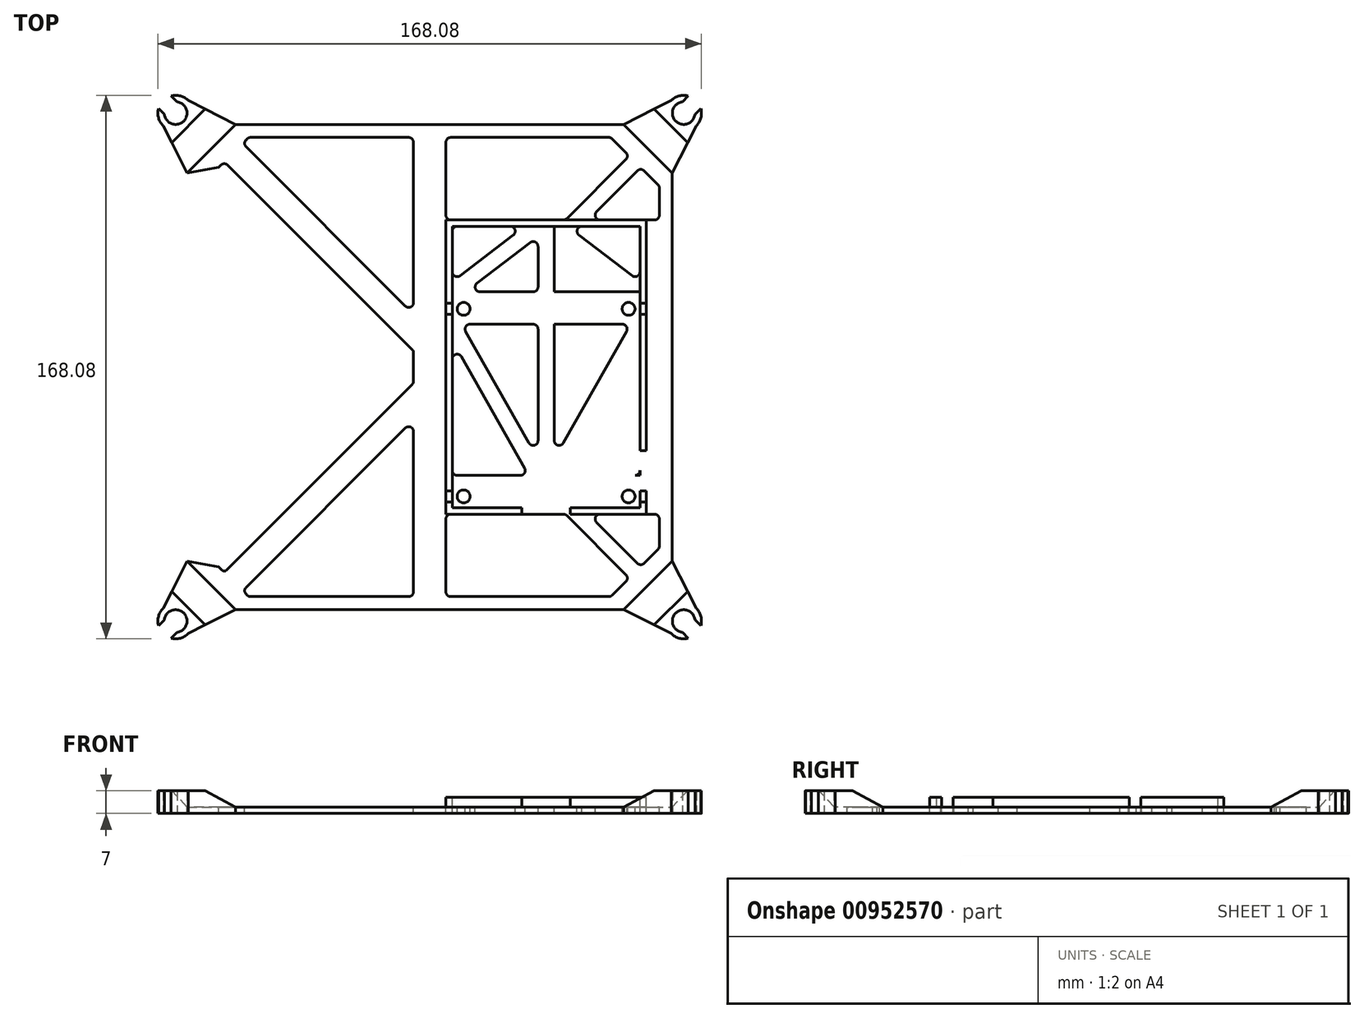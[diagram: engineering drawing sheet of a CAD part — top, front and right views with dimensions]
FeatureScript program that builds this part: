
annotation { "Feature Type Name" : "Feature", "Feature Type Description" : "" }
export const myFeature = defineFeature(function(context is Context, id is Id, definition is map)
    precondition{}
    {
        {
            var Q0;
            Q0=qCreatedBy(makeId("Top.planeOp"),FACE);
            var sketch = newSketch(context, id + "F0", { "sketchPlane" : qUnion([Q0])});
            skLineSegment(sketch, "E0.bottom", {"start": v(-75, 75) * mm, "end": v(75, 75) * mm});
            skLineSegment(sketch, "E0.top", {"start": v(-75, -75) * mm, "end": v(75, -75) * mm});
            skLineSegment(sketch, "E0.left", {"start": v(-75, 75) * mm, "end": v(-75, -75) * mm});
            skLineSegment(sketch, "E0.right", {"start": v(75, 75) * mm, "end": v(75, -75) * mm});
            skPoint(sketch, "E1", {"position": v(0, 75) * mm});
            skPoint(sketch, "E2", {"position": v(-75, 0) * mm});
            skSolve(sketch);
        }
        {
            var Q0;
            Q0=qSketchRegion(id+"F0",true);
            extrude(context, id + "F1", {"entities" : qUnion([Q0]), "depth" : 2 * mm, "offsetDistance" : 25 * mm});
        }
        {
            var Q0;
            Q0=makeQuery(id+"F1.opExtrude","CAP_FACE",FACE,{"disambiguationData":[OSD([sQuery(id+"F0.wireOp",EDGE,"E0.bottom"),sQuery(id+"F0.wireOp",EDGE,"E0.top"),sQuery(id+"F0.wireOp",EDGE,"E0.left"),sQuery(id+"F0.wireOp",EDGE,"E0.right")])],"isStart":false});
            var sketch = newSketch(context, id + "F2", { "sketchPlane" : qUnion([Q0])});
            skLineSegment(sketch, "E3.bottom", {"start": v(7, 43.5) * mm, "end": v(65, 43.5) * mm});
            skLineSegment(sketch, "E3.top", {"start": v(7, -43.5) * mm, "end": v(65, -43.5) * mm});
            skLineSegment(sketch, "E3.left", {"start": v(7, 43.5) * mm, "end": v(7, -43.5) * mm});
            skLineSegment(sketch, "E3.right", {"start": v(65, 43.5) * mm, "end": v(65, -43.5) * mm});
            skPoint(sketch, "E4", {"position": v(36, 43.5) * mm});
            skLineSegment(sketch, "E5.0", {"start": v(5, 45.5) * mm, "end": v(67, 45.5) * mm});
            skLineSegment(sketch, "E5.1", {"start": v(5, 45.5) * mm, "end": v(5, -45.5) * mm});
            skLineSegment(sketch, "E5.2", {"start": v(5, -45.5) * mm, "end": v(67, -45.5) * mm});
            skLineSegment(sketch, "E5.3", {"start": v(67, 45.5) * mm, "end": v(67, -45.5) * mm});
            skPoint(sketch, "E6", {"position": v(7, 0) * mm});
            skSolve(sketch);
        }
        {
            var Q0;
            Q0=qSketchRegion(id+"F2",true);
            extrude(context, id + "F3", {"entities" : qUnion([Q0]), "operationType" : NewBodyOperationType.ADD, "depth" : 3 * mm, "offsetDistance" : 25 * mm});
        }
        {
            var Q0;
            Q0=makeQuery(id+"F3.opExtrude","CAP_FACE",FACE,{"disambiguationData":[OSD([sQuery(id+"F2.wireOp",EDGE,"E3.bottom"),sQuery(id+"F2.wireOp",EDGE,"E3.top"),sQuery(id+"F2.wireOp",EDGE,"E3.left"),sQuery(id+"F2.wireOp",EDGE,"E3.right"),sQuery(id+"F2.wireOp",EDGE,"E5.0"),sQuery(id+"F2.wireOp",EDGE,"E5.1"),sQuery(id+"F2.wireOp",EDGE,"E5.2"),sQuery(id+"F2.wireOp",EDGE,"E5.3")])],"isStart":false});
            var sketch = newSketch(context, id + "F4", { "sketchPlane" : qUnion([Q0])});
            skLineSegment(sketch, "E7.bottom", {"start": v(28.5, -43.5) * mm, "end": v(43.5, -43.5) * mm});
            skLineSegment(sketch, "E7.top", {"start": v(28.5, -45.5) * mm, "end": v(43.5, -45.5) * mm});
            skLineSegment(sketch, "E7.left", {"start": v(28.5, -43.5) * mm, "end": v(28.5, -45.5) * mm});
            skLineSegment(sketch, "E7.right", {"start": v(43.5, -43.5) * mm, "end": v(43.5, -45.5) * mm});
            skLineSegment(sketch, "E8.bottom", {"start": v(67, -39.9) * mm, "end": v(65, -39.9) * mm});
            skLineSegment(sketch, "E8.top", {"start": v(67, -25.9) * mm, "end": v(65, -25.9) * mm});
            skLineSegment(sketch, "E8.left", {"start": v(67, -39.9) * mm, "end": v(67, -25.9) * mm});
            skLineSegment(sketch, "E8.right", {"start": v(65, -39.9) * mm, "end": v(65, -25.9) * mm});
            skPoint(sketch, "E9", {"position": v(36, -43.5) * mm});
            skPoint(sketch, "E10", {"position": v(36, -45.5) * mm});
            skPoint(sketch, "E11", {"position": v(65, -32.9) * mm});
            skSolve(sketch);
        }
        {
            var Q0;
            Q0=qSketchRegion(id+"F4",true);
            extrude(context, id + "F5", {"entities" : qUnion([Q0]), "operationType" : NewBodyOperationType.REMOVE, "oppositeDirection" : true, "depth" : 3 * mm, "offsetDistance" : 25 * mm});
        }
        {
            var Q0;
            {var subQ3=sQuery(id+"F4.wireOp",EDGE,"E7.bottom");Q0=makeQuery(id+"F4.imprint","IMPRINT",FACE,{"disambiguationData":[TD([[makeQuery(id+"F4.imprint","IMPRINT",EDGE,{"derivedFrom":subQ3}),1.0]])]});}
            var sketch = newSketch(context, id + "F6", { "sketchPlane" : qUnion([Q0])});
            skCircle(sketch, "E12", {"center": v(61.5, -40) * mm, "radius": 2 * mm});
            skCircle(sketch, "E13", {"center": v(61.5, 18) * mm, "radius": 2 * mm});
            skLineSegment(sketch, "E14", {"start": v(36, -43.5) * mm, "end": v(36, -14.74) * mm, "construction": true});
            skLineSegment(sketch, "E15.bottom", {"start": v(67, -41.75) * mm, "end": v(65, -41.75) * mm});
            skLineSegment(sketch, "E15.top", {"start": v(67, -38.25) * mm, "end": v(65, -38.25) * mm});
            skLineSegment(sketch, "E15.left", {"start": v(67, -41.75) * mm, "end": v(67, -38.25) * mm});
            skLineSegment(sketch, "E15.right", {"start": v(65, -41.75) * mm, "end": v(65, -38.25) * mm});
            skLineSegment(sketch, "E16.bottom", {"start": v(67, 19.75) * mm, "end": v(65, 19.75) * mm});
            skLineSegment(sketch, "E16.top", {"start": v(67, 16.25) * mm, "end": v(65, 16.25) * mm});
            skLineSegment(sketch, "E16.left", {"start": v(67, 19.75) * mm, "end": v(67, 16.25) * mm});
            skLineSegment(sketch, "E16.right", {"start": v(65, 19.75) * mm, "end": v(65, 16.25) * mm});
            skPoint(sketch, "E17", {"position": v(65, 18) * mm});
            skPoint(sketch, "E18", {"position": v(65, -40) * mm});
            skLineSegment(sketch, "E19.MirrorCS", {"start": v(5, -41.75) * mm, "end": v(7, -41.75) * mm});
            skLineSegment(sketch, "E20.MirrorCS", {"start": v(5, -41.75) * mm, "end": v(5, -38.25) * mm});
            skLineSegment(sketch, "E21.MirrorCS", {"start": v(7, -41.75) * mm, "end": v(7, -38.25) * mm});
            skLineSegment(sketch, "E22.MirrorCS", {"start": v(5, 16.25) * mm, "end": v(7, 16.25) * mm});
            skLineSegment(sketch, "E23.MirrorCS", {"start": v(5, -38.25) * mm, "end": v(7, -38.25) * mm});
            skLineSegment(sketch, "E24.MirrorCS", {"start": v(5, 19.75) * mm, "end": v(5, 16.25) * mm});
            skLineSegment(sketch, "E25.MirrorCS", {"start": v(7, 19.75) * mm, "end": v(7, 16.25) * mm});
            skLineSegment(sketch, "E26.MirrorCS", {"start": v(5, 19.75) * mm, "end": v(7, 19.75) * mm});
            skCircle(sketch, "E27.MirrorC", {"center": v(10.5, 18) * mm, "radius": 2 * mm});
            skCircle(sketch, "E28.MirrorC", {"center": v(10.5, -40) * mm, "radius": 2 * mm});
            skPoint(sketch, "E29.MirrorP", {"position": v(7, 18) * mm});
            skPoint(sketch, "E30.MirrorP", {"position": v(7, -40) * mm});
            skSolve(sketch);
        }
        {
            var Q0;
            Q0=qSketchRegion(id+"F6",true);
            extrude(context, id + "F7", {"entities" : qUnion([Q0]), "operationType" : NewBodyOperationType.REMOVE, "oppositeDirection" : true, "depth" : 25 * mm, "offsetDistance" : 25 * mm});
        }
        {
            var Q0;
            Q0=makeQuery(id+"F2.imprint","IMPRINT",FACE,{"disambiguationData":[TD([[makeQuery(id+"F2.imprint","IMPRINT",EDGE,{"derivedFrom":sQuery(id+"F2.wireOp",EDGE,"E5.0")}),1.0]])]});
            var sketch = newSketch(context, id + "F8", { "sketchPlane" : qUnion([Q0])});
            skLineSegment(sketch, "E31", {"start": v(75, 75) * mm, "end": v(78.54, 78.54) * mm, "construction": true});
            skLineSegment(sketch, "E32", {"start": v(78.12, 82.01) * mm, "end": v(79.96, 83.85) * mm});
            skLineSegment(sketch, "E33", {"start": v(79.96, 83.85) * mm, "end": v(83.85, 79.96) * mm, "construction": true});
            skLineSegment(sketch, "E34", {"start": v(83.85, 79.96) * mm, "end": v(82.01, 78.12) * mm});
            skLineSegment(sketch, "E35", {"start": v(82.01, 78.12) * mm, "end": v(78.12, 82.01) * mm, "construction": true});
            skPoint(sketch, "E36", {"position": v(80.07, 80.07) * mm});
            skLineSegment(sketch, "E37.MirrorCS", {"start": v(83.85, 79.96) * mm, "end": v(85.69, 81.8) * mm, "construction": true});
            skLineSegment(sketch, "E38.MirrorCS", {"start": v(81.8, 85.69) * mm, "end": v(79.96, 83.85) * mm, "construction": true});
            skLineSegment(sketch, "E39.MirrorCS", {"start": v(85.69, 81.8) * mm, "end": v(81.8, 85.69) * mm, "construction": true});
            skArc(sketch, "E40", {"start": v(79.96, 83.85) * mm, "mid": v(77.11, 83.85) * mm, "end": v(74.65, 82.42) * mm});
            skArc(sketch, "E41", {"start": v(83.85, 79.96) * mm, "mid": v(82.42, 82.42) * mm, "end": v(79.96, 83.85) * mm, "construction": true});
            skArc(sketch, "E42", {"start": v(82.01, 78.12) * mm, "mid": v(81.01, 81.01) * mm, "end": v(78.12, 82.01) * mm, "construction": true});
            skArc(sketch, "E43", {"start": v(78.12, 82.01) * mm, "mid": v(76.06, 76.06) * mm, "end": v(82.01, 78.12) * mm});
            skLineSegment(sketch, "E44", {"start": v(74.65, 82.42) * mm, "end": v(82.42, 74.65) * mm, "construction": true});
            skLineSegment(sketch, "E45", {"start": v(74.65, 82.42) * mm, "end": v(60, 75) * mm});
            skLineSegment(sketch, "E46.MirrorCS", {"start": v(82.42, 74.65) * mm, "end": v(75, 60) * mm});
            skArc(sketch, "E47", {"start": v(82.42, 74.65) * mm, "mid": v(83.85, 77.11) * mm, "end": v(83.85, 79.96) * mm});
            skArc(sketch, "E48", {"start": v(74.65, 82.42) * mm, "mid": v(74.65, 74.65) * mm, "end": v(82.42, 74.65) * mm, "construction": true});
            skLineSegment(sketch, "E49.2.8", {"start": v(-75, -75) * mm, "end": v(75, 75) * mm, "construction": true});
            skLineSegment(sketch, "E50", {"start": v(60, 75) * mm, "end": v(75, 60) * mm});
            skLineSegment(sketch, "E51.1.0", {"start": v(-74.65, 82.42) * mm, "end": v(-60, 75) * mm});
            skArc(sketch, "E51.1.1", {"start": v(-82.42, 74.65) * mm, "mid": v(-74.65, 74.65) * mm, "end": v(-74.65, 82.42) * mm, "construction": true});
            skLineSegment(sketch, "E51.1.2", {"start": v(-82.42, 74.65) * mm, "end": v(-75, 60) * mm});
            skLineSegment(sketch, "E51.1.3", {"start": v(-75, 60) * mm, "end": v(-60, 75) * mm});
            skPoint(sketch, "E51.1.4", {"position": v(-78.54, 78.54) * mm});
            skArc(sketch, "E51.1.5", {"start": v(-82.01, 78.12) * mm, "mid": v(-76.06, 76.06) * mm, "end": v(-78.12, 82.01) * mm});
            skLineSegment(sketch, "E51.1.6", {"start": v(-81.8, 85.69) * mm, "end": v(-85.69, 81.8) * mm, "construction": true});
            skPoint(sketch, "E51.1.7", {"position": v(-80.07, 80.07) * mm});
            skLineSegment(sketch, "E51.1.8", {"start": v(-75, 75) * mm, "end": v(-78.54, 78.54) * mm, "construction": true});
            skLineSegment(sketch, "E51.1.9", {"start": v(-82.42, 74.65) * mm, "end": v(-74.65, 82.42) * mm, "construction": true});
            skArc(sketch, "E51.1.10", {"start": v(-78.12, 82.01) * mm, "mid": v(-81.01, 81.01) * mm, "end": v(-82.01, 78.12) * mm, "construction": true});
            skArc(sketch, "E51.1.11", {"start": v(-74.65, 82.42) * mm, "mid": v(-77.11, 83.85) * mm, "end": v(-79.96, 83.85) * mm});
            skArc(sketch, "E51.1.12", {"start": v(-83.85, 79.96) * mm, "mid": v(-83.85, 77.11) * mm, "end": v(-82.42, 74.65) * mm});
            skLineSegment(sketch, "E51.1.13", {"start": v(-78.12, 82.01) * mm, "end": v(-82.01, 78.12) * mm, "construction": true});
            skLineSegment(sketch, "E51.1.14", {"start": v(-83.85, 79.96) * mm, "end": v(-79.96, 83.85) * mm, "construction": true});
            skLineSegment(sketch, "E51.1.15", {"start": v(-85.69, 81.8) * mm, "end": v(-83.85, 79.96) * mm, "construction": true});
            skLineSegment(sketch, "E51.1.16", {"start": v(-79.96, 83.85) * mm, "end": v(-78.12, 82.01) * mm});
            skLineSegment(sketch, "E51.1.17", {"start": v(-79.96, 83.85) * mm, "end": v(-81.8, 85.69) * mm, "construction": true});
            skArc(sketch, "E51.1.18", {"start": v(-79.96, 83.85) * mm, "mid": v(-82.42, 82.42) * mm, "end": v(-83.85, 79.96) * mm, "construction": true});
            skLineSegment(sketch, "E51.1.19", {"start": v(-82.01, 78.12) * mm, "end": v(-83.85, 79.96) * mm});
            skLineSegment(sketch, "E51.2.0", {"start": v(-82.42, -74.65) * mm, "end": v(-75, -60) * mm});
            skArc(sketch, "E51.2.1", {"start": v(-74.65, -82.42) * mm, "mid": v(-74.65, -74.65) * mm, "end": v(-82.42, -74.65) * mm, "construction": true});
            skLineSegment(sketch, "E51.2.2", {"start": v(-74.65, -82.42) * mm, "end": v(-60, -75) * mm});
            skLineSegment(sketch, "E51.2.3", {"start": v(-60, -75) * mm, "end": v(-75, -60) * mm});
            skPoint(sketch, "E51.2.4", {"position": v(-78.54, -78.54) * mm});
            skArc(sketch, "E51.2.5", {"start": v(-78.12, -82.01) * mm, "mid": v(-76.06, -76.06) * mm, "end": v(-82.01, -78.12) * mm});
            skLineSegment(sketch, "E51.2.6", {"start": v(-85.69, -81.8) * mm, "end": v(-81.8, -85.69) * mm, "construction": true});
            skPoint(sketch, "E51.2.7", {"position": v(-80.07, -80.07) * mm});
            skLineSegment(sketch, "E51.2.8", {"start": v(-75, -75) * mm, "end": v(-78.54, -78.54) * mm, "construction": true});
            skLineSegment(sketch, "E51.2.9", {"start": v(-74.65, -82.42) * mm, "end": v(-82.42, -74.65) * mm, "construction": true});
            skArc(sketch, "E51.2.10", {"start": v(-82.01, -78.12) * mm, "mid": v(-81.01, -81.01) * mm, "end": v(-78.12, -82.01) * mm, "construction": true});
            skArc(sketch, "E51.2.11", {"start": v(-82.42, -74.65) * mm, "mid": v(-83.85, -77.11) * mm, "end": v(-83.85, -79.96) * mm});
            skArc(sketch, "E51.2.12", {"start": v(-79.96, -83.85) * mm, "mid": v(-77.11, -83.85) * mm, "end": v(-74.65, -82.42) * mm});
            skLineSegment(sketch, "E51.2.13", {"start": v(-82.01, -78.12) * mm, "end": v(-78.12, -82.01) * mm, "construction": true});
            skLineSegment(sketch, "E51.2.14", {"start": v(-79.96, -83.85) * mm, "end": v(-83.85, -79.96) * mm, "construction": true});
            skLineSegment(sketch, "E51.2.15", {"start": v(-81.8, -85.69) * mm, "end": v(-79.96, -83.85) * mm, "construction": true});
            skLineSegment(sketch, "E51.2.16", {"start": v(-83.85, -79.96) * mm, "end": v(-82.01, -78.12) * mm});
            skLineSegment(sketch, "E51.2.17", {"start": v(-83.85, -79.96) * mm, "end": v(-85.69, -81.8) * mm, "construction": true});
            skArc(sketch, "E51.2.18", {"start": v(-83.85, -79.96) * mm, "mid": v(-82.42, -82.42) * mm, "end": v(-79.96, -83.85) * mm, "construction": true});
            skLineSegment(sketch, "E51.2.19", {"start": v(-78.12, -82.01) * mm, "end": v(-79.96, -83.85) * mm});
            skPoint(sketch, "E51.center", {"position": v(0, 0) * mm});
            skLineSegment(sketch, "E52.2.3.0", {"start": v(74.65, -82.42) * mm, "end": v(60, -75) * mm});
            skArc(sketch, "E52.3.3.0", {"start": v(82.42, -74.65) * mm, "mid": v(74.65, -74.65) * mm, "end": v(74.65, -82.42) * mm, "construction": true});
            skLineSegment(sketch, "E52.7.3.0", {"start": v(82.42, -74.65) * mm, "end": v(75, -60) * mm});
            skLineSegment(sketch, "E52.10.3.0", {"start": v(75, -60) * mm, "end": v(60, -75) * mm});
            skPoint(sketch, "E52.13.3.0", {"position": v(78.54, -78.54) * mm});
            skArc(sketch, "E52.14.3.0", {"start": v(82.01, -78.12) * mm, "mid": v(76.06, -76.06) * mm, "end": v(78.12, -82.01) * mm});
            skLineSegment(sketch, "E52.18.3.0", {"start": v(81.8, -85.69) * mm, "end": v(85.69, -81.8) * mm, "construction": true});
            skPoint(sketch, "E52.21.3.0", {"position": v(80.07, -80.07) * mm});
            skLineSegment(sketch, "E52.22.3.0", {"start": v(75, -75) * mm, "end": v(78.54, -78.54) * mm, "construction": true});
            skLineSegment(sketch, "E52.25.3.0", {"start": v(82.42, -74.65) * mm, "end": v(74.65, -82.42) * mm, "construction": true});
            skArc(sketch, "E52.28.3.0", {"start": v(78.12, -82.01) * mm, "mid": v(81.01, -81.01) * mm, "end": v(82.01, -78.12) * mm, "construction": true});
            skArc(sketch, "E52.32.3.0", {"start": v(74.65, -82.42) * mm, "mid": v(77.11, -83.85) * mm, "end": v(79.96, -83.85) * mm});
            skArc(sketch, "E52.36.3.0", {"start": v(83.85, -79.96) * mm, "mid": v(83.85, -77.11) * mm, "end": v(82.42, -74.65) * mm});
            skLineSegment(sketch, "E52.40.3.0", {"start": v(78.12, -82.01) * mm, "end": v(82.01, -78.12) * mm, "construction": true});
            skLineSegment(sketch, "E52.43.3.0", {"start": v(83.85, -79.96) * mm, "end": v(79.96, -83.85) * mm, "construction": true});
            skLineSegment(sketch, "E52.46.3.0", {"start": v(85.69, -81.8) * mm, "end": v(83.85, -79.96) * mm, "construction": true});
            skLineSegment(sketch, "E52.49.3.0", {"start": v(79.96, -83.85) * mm, "end": v(78.12, -82.01) * mm});
            skLineSegment(sketch, "E52.52.3.0", {"start": v(79.96, -83.85) * mm, "end": v(81.8, -85.69) * mm, "construction": true});
            skArc(sketch, "E52.55.3.0", {"start": v(79.96, -83.85) * mm, "mid": v(82.42, -82.42) * mm, "end": v(83.85, -79.96) * mm, "construction": true});
            skLineSegment(sketch, "E52.59.3.0", {"start": v(82.01, -78.12) * mm, "end": v(83.85, -79.96) * mm});
            skSolve(sketch);
        }
        {
            var Q0;
            Q0=qSketchRegion(id+"F8",true);
            extrude(context, id + "F9", {"entities" : qUnion([Q0]), "operationType" : NewBodyOperationType.ADD, "depth" : 5 * mm, "offsetDistance" : 25 * mm, "hasSecondDirection" : true, "secondDirectionOppositeDirection" : true, "secondDirectionDepth" : 2 * mm});
        }
        {
            var Q0;
            Q0=qSketchRegion(id+"F8",true);
            extrude(context, id + "F10", {"entities" : qUnion([Q0]), "operationType" : NewBodyOperationType.ADD, "depth" : 5 * mm, "offsetDistance" : 25 * mm});
        }
        {
            var Q0;
            Q0=qSketchRegion(id+"F8",true);
            extrude(context, id + "F11", {"entities" : qUnion([Q0]), "operationType" : NewBodyOperationType.ADD, "depth" : 5 * mm, "offsetDistance" : 25 * mm});
        }
        {
            var Q0;
            Q0=makeQuery(id+"F9.opExtrude","CAP_EDGE",EDGE,{"disambiguationData":[OSD([sQuery(id+"F8.wireOp",EDGE,"E51.1.3")])],"isStart":false});
            var Q1;
            Q1=makeQuery(id+"F9.opExtrude","CAP_EDGE",EDGE,{"disambiguationData":[OSD([sQuery(id+"F8.wireOp",EDGE,"E50")])],"isStart":false});
            var Q2;
            Q2=makeQuery(id+"F9.opExtrude","CAP_EDGE",EDGE,{"disambiguationData":[OSD([sQuery(id+"F8.wireOp",EDGE,"E52.10.3.0")])],"isStart":false});
            var Q3;
            Q3=makeQuery(id+"F9.opExtrude","CAP_EDGE",EDGE,{"disambiguationData":[OSD([sQuery(id+"F8.wireOp",EDGE,"E51.2.3")])],"isStart":false});
            chamfer(context, id + "F12", {"entities" : qUnion([Q0, Q1, Q2, Q3]), "chamferType" : ChamferType.TWO_OFFSETS, "width1" : 10 * mm, "oppositeDirection" : false, "width2" : 5 * mm, "tangentPropagation" : true});
        }
        {
            var Q0;
            Q0=makeQuery(id+"F2.imprint","IMPRINT",FACE,{"disambiguationData":[TD([[makeQuery(id+"F2.imprint","IMPRINT",EDGE,{"derivedFrom":sQuery(id+"F2.wireOp",EDGE,"E5.0")}),1.0]])]});
            var sketch = newSketch(context, id + "F13", { "sketchPlane" : qUnion([Q0])});
            skLineSegment(sketch, "E53", {"start": v(-71, -56) * mm, "end": v(-71, 56) * mm, "construction": true});
            skLineSegment(sketch, "E54", {"start": v(-56.78, 70.22) * mm, "end": v(-56, 71) * mm, "construction": true});
            skLineSegment(sketch, "E55", {"start": v(-75, 60) * mm, "end": v(60, -75) * mm, "construction": true});
            skLineSegment(sketch, "E56", {"start": v(-75, -60) * mm, "end": v(60, 75) * mm, "construction": true});
            skLineSegment(sketch, "E57.1.0", {"start": v(-56, -71) * mm, "end": v(-71, -56) * mm, "construction": true});
            skLineSegment(sketch, "E57.1.1", {"start": v(56, -71) * mm, "end": v(-56, -71) * mm, "construction": true});
            skLineSegment(sketch, "E57.2.0", {"start": v(71, -56) * mm, "end": v(56, -71) * mm, "construction": true});
            skLineSegment(sketch, "E57.2.1", {"start": v(71, 56) * mm, "end": v(71, -56) * mm, "construction": true});
            skLineSegment(sketch, "E57.3.0", {"start": v(56, 71) * mm, "end": v(71, 56) * mm, "construction": true});
            skLineSegment(sketch, "E57.3.1", {"start": v(-56, 71) * mm, "end": v(-6.5, 71) * mm, "construction": true});
            skPoint(sketch, "E57.center", {"position": v(0, 0) * mm});
            skLineSegment(sketch, "E58", {"start": v(-71, 56) * mm, "end": v(-71, -56) * mm});
            skLineSegment(sketch, "E59", {"start": v(-5, 69.5) * mm, "end": v(-5, 19.94) * mm, "construction": true});
            skLineSegment(sketch, "E60", {"start": v(5, 71) * mm, "end": v(5, 45.5) * mm});
            skLineSegment(sketch, "E61", {"start": v(5, -45.5) * mm, "end": v(5, -71) * mm});
            skLineSegment(sketch, "E62", {"start": v(-71, 5) * mm, "end": v(-8.54, 5) * mm});
            skLineSegment(sketch, "E63", {"start": v(-71, -5) * mm, "end": v(0, -5) * mm});
            skLineSegment(sketch, "E64", {"start": v(-56.78, 68.1) * mm, "end": v(-7.56, 18.87) * mm});
            skLineSegment(sketch, "E65", {"start": v(-65.27, 61.73) * mm, "end": v(-8.54, 5) * mm, "construction": true});
            skPoint(sketch, "E66", {"position": v(-63.5, 63.5) * mm});
            skLineSegment(sketch, "E67", {"start": v(-63.5, 63.5) * mm, "end": v(75.2, -75.2) * mm, "construction": true});
            skLineSegment(sketch, "E68", {"start": v(-5, 71) * mm, "end": v(-56, 71) * mm});
            skLineSegment(sketch, "E69", {"start": v(-57.84, 69.16) * mm, "end": v(-56, 71) * mm});
            skLineSegment(sketch, "E70", {"start": v(-65.27, 61.73) * mm, "end": v(-71, 56) * mm});
            skLineSegment(sketch, "E71", {"start": v(-71, 5) * mm, "end": v(-71, 56) * mm});
            skLineSegment(sketch, "E72", {"start": v(0, 0) * mm, "end": v(-75, 0) * mm, "construction": true});
            skLineSegment(sketch, "E73.MirrorCS", {"start": v(-71, -5) * mm, "end": v(-71, -56) * mm});
            skLineSegment(sketch, "E74.MirrorCS", {"start": v(-65.27, -61.73) * mm, "end": v(-71, -56) * mm});
            skLineSegment(sketch, "E75.MirrorCS", {"start": v(-57.84, -69.16) * mm, "end": v(-56, -71) * mm});
            skLineSegment(sketch, "E76.MirrorCS", {"start": v(-5, -71) * mm, "end": v(-56, -71) * mm});
            skLineSegment(sketch, "E77.MirrorCS", {"start": v(-71, -56) * mm, "end": v(-71, 56) * mm});
            skLineSegment(sketch, "E78.MirrorCS", {"start": v(-57.84, -69.16) * mm, "end": v(-1.11, -12.42) * mm});
            skPoint(sketch, "E79.MirrorP", {"position": v(-63.5, -63.5) * mm});
            skLineSegment(sketch, "E80.MirrorCS", {"start": v(-56, -71) * mm, "end": v(56, -71) * mm, "construction": true});
            skLineSegment(sketch, "E81.MirrorCS", {"start": v(-71, -56) * mm, "end": v(-56, -71) * mm, "construction": true});
            skLineSegment(sketch, "E82.MirrorCS", {"start": v(-63.5, -63.5) * mm, "end": v(75.2, 75.2) * mm, "construction": true});
            skLineSegment(sketch, "E83.MirrorCS", {"start": v(-5, -71) * mm, "end": v(-5, 8.54) * mm});
            skLineSegment(sketch, "E84", {"start": v(-5, 8.54) * mm, "end": v(-5, 71) * mm});
            skLineSegment(sketch, "E85", {"start": v(-5, 8.54) * mm, "end": v(-5, 71) * mm, "construction": true});
            skLineSegment(sketch, "E86", {"start": v(-1.11, -12.42) * mm, "end": v(-1.11, -74.89) * mm, "construction": true});
            skLineSegment(sketch, "E87", {"start": v(5, -71) * mm, "end": v(56, -71) * mm});
            skLineSegment(sketch, "E88", {"start": v(5, 71) * mm, "end": v(56, 71) * mm});
            skLineSegment(sketch, "E89", {"start": v(56, 71) * mm, "end": v(61.73, 65.27) * mm});
            skLineSegment(sketch, "E90", {"start": v(61.73, 65.27) * mm, "end": v(41.96, 45.5) * mm});
            skLineSegment(sketch, "E91", {"start": v(41.96, 45.5) * mm, "end": v(5, 45.5) * mm});
            skLineSegment(sketch, "E92", {"start": v(5, -45.5) * mm, "end": v(41.96, -45.5) * mm});
            skLineSegment(sketch, "E93", {"start": v(41.96, -45.5) * mm, "end": v(61.73, -65.27) * mm});
            skLineSegment(sketch, "E94", {"start": v(61.73, -65.27) * mm, "end": v(56, -71) * mm});
            skLineSegment(sketch, "E95", {"start": v(65.27, 61.73) * mm, "end": v(49.04, 45.5) * mm});
            skLineSegment(sketch, "E96", {"start": v(49.04, 45.5) * mm, "end": v(71, 45.5) * mm});
            skLineSegment(sketch, "E97", {"start": v(71, 45.5) * mm, "end": v(71, 56) * mm});
            skLineSegment(sketch, "E98", {"start": v(65.27, 61.73) * mm, "end": v(71, 56) * mm});
            skLineSegment(sketch, "E99", {"start": v(49.04, -45.5) * mm, "end": v(65.27, -61.73) * mm});
            skLineSegment(sketch, "E100", {"start": v(65.27, -61.73) * mm, "end": v(71, -56) * mm});
            skLineSegment(sketch, "E101", {"start": v(71, -45.5) * mm, "end": v(49.04, -45.5) * mm});
            skLineSegment(sketch, "E102", {"start": v(71, -45.5) * mm, "end": v(71, -56) * mm});
            skPoint(sketch, "E103.newPointA", {"position": v(56, 71) * mm});
            skPoint(sketch, "E103.newPointB", {"position": v(-5, 71) * mm});
            skArc(sketch, "E103.filletArc", {"start": v(-5, 69.5) * mm, "mid": v(-5.44, 70.56) * mm, "end": v(-6.5, 71) * mm, "construction": true});
            skPoint(sketch, "E104.newPointA", {"position": v(-71, 56) * mm});
            skPoint(sketch, "E104.newPointB", {"position": v(-57.84, 69.16) * mm});
            skArc(sketch, "E104.filletArc", {"start": v(-56.78, 70.22) * mm, "mid": v(-57.22, 69.16) * mm, "end": v(-56.78, 68.1) * mm});
            skPoint(sketch, "E105.newPointA", {"position": v(-5, -71) * mm});
            skPoint(sketch, "E105.newPointB", {"position": v(-1.11, 12.42) * mm});
            skArc(sketch, "E105.filletArc", {"start": v(-7.56, 18.87) * mm, "mid": v(-5.93, 18.55) * mm, "end": v(-5, 19.94) * mm});
            skLineSegment(sketch, "E106", {"start": v(-65.27, 61.73) * mm, "end": v(-63.5, 63.5) * mm});
            skPoint(sketch, "E107.startSnap0", {"position": v(-7.5, 7.5) * mm});
            skLineSegment(sketch, "E108", {"start": v(-5, 19.94) * mm, "end": v(-5, 5) * mm});
            skLineSegment(sketch, "E109", {"start": v(-5, 5) * mm, "end": v(-63.5, 63.5) * mm});
            skLineSegment(sketch, "E110", {"start": v(-65.27, -61.73) * mm, "end": v(-63.5, -63.5) * mm});
            skLineSegment(sketch, "E111", {"start": v(-63.5, -63.5) * mm, "end": v(-5, -5) * mm});
            skSolve(sketch);
        }
        {
            var Q0;
            {var subQ4=sQuery(id+"F13.wireOp",EDGE,"E95");var subQ5=sQuery(id+"F13.wireOp",EDGE,"E74.MirrorCS");var subQ13=sQuery(id+"F13.wireOp",EDGE,"E70");var subQ16=sQuery(id+"F13.wireOp",EDGE,"E75.MirrorCS");var subQ22=sQuery(id+"F13.wireOp",EDGE,"E99");Q0=qUnion([makeQuery(id+"F13.imprint","IMPRINT",FACE,{"disambiguationData":[TD([[makeQuery(id+"F13.imprint","IMPRINT",EDGE,{"derivedFrom":sQuery(id+"F13.wireOp",EDGE,"E64")}),1.0]])]}),makeQuery(id+"F13.imprint","IMPRINT",FACE,{"disambiguationData":[TD([[makeQuery(id+"F13.imprint","IMPRINT",EDGE,{"derivedFrom":sQuery(id+"F13.wireOp",EDGE,"E60")}),1.0]])]}),makeQuery(id+"F13.imprint","IMPRINT",FACE,{"disambiguationData":[TD([[makeQuery(id+"F13.imprint","IMPRINT",EDGE,{"derivedFrom":subQ22}),1.0]])]}),makeQuery(id+"F13.imprint","IMPRINT",FACE,{"disambiguationData":[TD([[makeQuery(id+"F13.imprint","IMPRINT",EDGE,{"derivedFrom":subQ16}),1.0]])]}),makeQuery(id+"F13.imprint","IMPRINT",FACE,{"disambiguationData":[TD([[makeQuery(id+"F13.imprint","IMPRINT",EDGE,{"derivedFrom":sQuery(id+"F13.wireOp",EDGE,"E61")}),1.0]])]}),makeQuery(id+"F13.imprint","IMPRINT",FACE,{"disambiguationData":[TD([[makeQuery(id+"F13.imprint","IMPRINT",EDGE,{"derivedFrom":subQ13}),1.0]])]}),makeQuery(id+"F13.imprint","IMPRINT",FACE,{"disambiguationData":[TD([[makeQuery(id+"F13.imprint","IMPRINT",EDGE,{"derivedFrom":subQ5}),-1.0]])]}),makeQuery(id+"F13.imprint","IMPRINT",FACE,{"disambiguationData":[TD([[makeQuery(id+"F13.imprint","IMPRINT",EDGE,{"derivedFrom":subQ4}),1.0]])]})]);}
            extrude(context, id + "F14", {"entities" : qUnion([Q0]), "operationType" : NewBodyOperationType.REMOVE, "oppositeDirection" : true, "depth" : 25 * mm, "offsetDistance" : 25 * mm});
        }
        {
            var Q0;
            {var subQ3=sQuery(id+"F4.wireOp",EDGE,"E7.bottom");Q0=makeQuery(id+"F4.imprint","IMPRINT",FACE,{"disambiguationData":[TD([[makeQuery(id+"F4.imprint","IMPRINT",EDGE,{"derivedFrom":subQ3}),1.0]])]});}
            var sketch = newSketch(context, id + "F15", { "sketchPlane" : qUnion([Q0])});
            skLineSegment(sketch, "E112", {"start": v(7, 23.25) * mm, "end": v(11.12, 23.25) * mm, "construction": true});
            skLineSegment(sketch, "E113", {"start": v(7, 13.25) * mm, "end": v(9.87, 13.25) * mm, "construction": true});
            skLineSegment(sketch, "E114", {"start": v(33.5, 43.5) * mm, "end": v(33.5, 40.35) * mm, "construction": true});
            skLineSegment(sketch, "E115", {"start": v(38.5, 43.5) * mm, "end": v(38.5, 23.25) * mm});
            skLineSegment(sketch, "E116", {"start": v(8.5, -33.5) * mm, "end": v(28.05, -33.5) * mm});
            skLineSegment(sketch, "E117", {"start": v(33.5, 11.75) * mm, "end": v(33.5, -22.74) * mm});
            skLineSegment(sketch, "E118", {"start": v(38.5, 13.25) * mm, "end": v(38.5, -33.5) * mm});
            skLineSegment(sketch, "E119", {"start": v(7, 23.25) * mm, "end": v(7, 13.25) * mm, "construction": true});
            skPoint(sketch, "E120", {"position": v(7, 18.25) * mm});
            skLineSegment(sketch, "E121", {"start": v(33.5, 43.5) * mm, "end": v(38.5, 43.5) * mm, "construction": true});
            skPoint(sketch, "E122", {"position": v(36, 43.5) * mm});
            skLineSegment(sketch, "E123", {"start": v(38.5, 23.25) * mm, "end": v(65, 23.25) * mm});
            skLineSegment(sketch, "E124", {"start": v(33.5, 23.25) * mm, "end": v(38.5, 23.25) * mm, "construction": true});
            skLineSegment(sketch, "E125", {"start": v(33.5, 13.25) * mm, "end": v(38.5, 13.25) * mm, "construction": true});
            skLineSegment(sketch, "E126", {"start": v(38.5, 13.25) * mm, "end": v(65, 13.25) * mm});
            skLineSegment(sketch, "E127", {"start": v(38.5, -33.5) * mm, "end": v(38.5, -33.5) * mm});
            skLineSegment(sketch, "E128", {"start": v(33.5, -33.5) * mm, "end": v(38.5, -33.5) * mm, "construction": true});
            skLineSegment(sketch, "E129", {"start": v(38.5, -33.5) * mm, "end": v(65, -33.5) * mm});
            skLineSegment(sketch, "E130", {"start": v(11.14, 11.01) * mm, "end": v(30.7, -23.48) * mm});
            skLineSegment(sketch, "E131", {"start": v(9.8, 3.23) * mm, "end": v(29.36, -31.26) * mm});
            skLineSegment(sketch, "E132", {"start": v(7, 13.25) * mm, "end": v(33.5, -33.5) * mm, "construction": true});
            skLineSegment(sketch, "E133", {"start": v(12.45, 13.25) * mm, "end": v(32, 13.25) * mm});
            skLineSegment(sketch, "E134", {"start": v(7, 2.5) * mm, "end": v(7, -32) * mm});
            skPoint(sketch, "E135.visualSharp", {"position": v(7, 8.18) * mm});
            skArc(sketch, "E135.filletArc", {"start": v(9.8, 3.23) * mm, "mid": v(8.12, 3.94) * mm, "end": v(7, 2.5) * mm});
            skArc(sketch, "E136.filletArc", {"start": v(28.05, -33.5) * mm, "mid": v(29.35, -32.76) * mm, "end": v(29.36, -31.26) * mm});
            skPoint(sketch, "E137.visualSharp", {"position": v(7, -33.5) * mm});
            skArc(sketch, "E137.filletArc", {"start": v(7, -32) * mm, "mid": v(7.44, -33.06) * mm, "end": v(8.5, -33.5) * mm});
            skPoint(sketch, "E138.visualSharp", {"position": v(9.87, 13.25) * mm});
            skArc(sketch, "E138.filletArc", {"start": v(12.45, 13.25) * mm, "mid": v(11.15, 12.5) * mm, "end": v(11.14, 11.01) * mm});
            skPoint(sketch, "E139.visualSharp", {"position": v(33.5, 13.25) * mm});
            skArc(sketch, "E139.filletArc", {"start": v(33.5, 11.75) * mm, "mid": v(33.06, 12.81) * mm, "end": v(32, 13.25) * mm});
            skArc(sketch, "E140.filletArc", {"start": v(30.7, -23.48) * mm, "mid": v(32.38, -24.2) * mm, "end": v(33.5, -22.74) * mm});
            skLineSegment(sketch, "E141", {"start": v(36, -43.5) * mm, "end": v(36, -5.37) * mm, "construction": true});
            skArc(sketch, "E142.MirrorCS", {"start": v(65, -32) * mm, "mid": v(64.56, -33.06) * mm, "end": v(63.5, -33.5) * mm});
            skArc(sketch, "E143.MirrorCS", {"start": v(62.2, 3.23) * mm, "mid": v(63.88, 3.94) * mm, "end": v(65, 2.5) * mm});
            skArc(sketch, "E144.MirrorCS", {"start": v(43.95, -33.5) * mm, "mid": v(42.65, -32.76) * mm, "end": v(42.64, -31.26) * mm});
            skArc(sketch, "E145.MirrorCS", {"start": v(38.5, 11.75) * mm, "mid": v(38.94, 12.81) * mm, "end": v(40, 13.25) * mm});
            skLineSegment(sketch, "E146.MirrorCS", {"start": v(38.5, 13.25) * mm, "end": v(33.5, 13.25) * mm, "construction": true});
            skLineSegment(sketch, "E147.MirrorCS", {"start": v(65, 13.25) * mm, "end": v(62.13, 13.25) * mm, "construction": true});
            skArc(sketch, "E148.MirrorCS", {"start": v(59.55, 13.25) * mm, "mid": v(60.85, 12.5) * mm, "end": v(60.86, 11.01) * mm});
            skLineSegment(sketch, "E149.MirrorCS", {"start": v(38.5, -33.5) * mm, "end": v(33.5, -33.5) * mm, "construction": true});
            skArc(sketch, "E150.MirrorCS", {"start": v(41.3, -23.48) * mm, "mid": v(39.62, -24.2) * mm, "end": v(38.5, -22.74) * mm});
            skLineSegment(sketch, "E151.MirrorCS", {"start": v(65, 13.25) * mm, "end": v(38.5, -33.5) * mm, "construction": true});
            skLineSegment(sketch, "E152.MirrorCS", {"start": v(65, 23.25) * mm, "end": v(65, 13.25) * mm, "construction": true});
            skLineSegment(sketch, "E153.MirrorCS", {"start": v(60.86, 11.01) * mm, "end": v(41.3, -23.48) * mm});
            skPoint(sketch, "E154.MirrorP", {"position": v(65, 18.25) * mm});
            skLineSegment(sketch, "E155.MirrorCS", {"start": v(62.2, 3.23) * mm, "end": v(42.64, -31.26) * mm});
            skPoint(sketch, "E156.MirrorP", {"position": v(38.5, 13.25) * mm});
            skPoint(sketch, "E157.MirrorP", {"position": v(65, 8.18) * mm});
            skLineSegment(sketch, "E158.MirrorCS", {"start": v(63.5, -33.5) * mm, "end": v(43.95, -33.5) * mm});
            skLineSegment(sketch, "E159.MirrorCS", {"start": v(59.55, 13.25) * mm, "end": v(40, 13.25) * mm});
            skPoint(sketch, "E160.MirrorP", {"position": v(65, -33.5) * mm});
            skLineSegment(sketch, "E161.MirrorCS", {"start": v(38.5, 11.75) * mm, "end": v(38.5, -22.74) * mm});
            skPoint(sketch, "E162.MirrorP", {"position": v(62.13, 13.25) * mm});
            skLineSegment(sketch, "E163.MirrorCS", {"start": v(65, 2.5) * mm, "end": v(65, -32) * mm});
            skLineSegment(sketch, "E164", {"start": v(31.09, 38.51) * mm, "end": v(14.64, 25.94) * mm});
            skLineSegment(sketch, "E165", {"start": v(33.5, 43.5) * mm, "end": v(7, 23.25) * mm, "construction": true});
            skLineSegment(sketch, "E166", {"start": v(33.5, 37.32) * mm, "end": v(33.5, 24.75) * mm});
            skLineSegment(sketch, "E167", {"start": v(15.55, 23.25) * mm, "end": v(32, 23.25) * mm});
            skPoint(sketch, "E168.visualSharp", {"position": v(33.5, 40.35) * mm});
            skArc(sketch, "E168.filletArc", {"start": v(33.5, 37.32) * mm, "mid": v(32.66, 38.66) * mm, "end": v(31.09, 38.51) * mm});
            skPoint(sketch, "E169.visualSharp", {"position": v(33.5, 23.25) * mm});
            skArc(sketch, "E169.filletArc", {"start": v(32, 23.25) * mm, "mid": v(33.06, 23.69) * mm, "end": v(33.5, 24.75) * mm});
            skPoint(sketch, "E170.visualSharp", {"position": v(11.12, 23.25) * mm});
            skArc(sketch, "E170.filletArc", {"start": v(14.64, 25.94) * mm, "mid": v(14.13, 24.27) * mm, "end": v(15.55, 23.25) * mm});
            skPoint(sketch, "E171", {"position": v(20.25, 33.38) * mm});
            skLineSegment(sketch, "E172.1.0", {"start": v(7, 29.43) * mm, "end": v(7, 42) * mm});
            skArc(sketch, "E172.1.1", {"start": v(7, 29.43) * mm, "mid": v(7.84, 28.09) * mm, "end": v(9.41, 28.24) * mm});
            skLineSegment(sketch, "E172.1.2", {"start": v(9.41, 28.24) * mm, "end": v(25.86, 40.8) * mm});
            skArc(sketch, "E172.1.3", {"start": v(25.86, 40.8) * mm, "mid": v(26.37, 42.48) * mm, "end": v(24.95, 43.5) * mm});
            skLineSegment(sketch, "E172.1.4", {"start": v(24.95, 43.5) * mm, "end": v(8.5, 43.5) * mm});
            skArc(sketch, "E172.1.5", {"start": v(8.5, 43.5) * mm, "mid": v(7.44, 43.06) * mm, "end": v(7, 42) * mm});
            skLineSegment(sketch, "E173", {"start": v(36, 43.5) * mm, "end": v(36, 23.25) * mm, "construction": true});
            skArc(sketch, "E174.MirrorCS", {"start": v(40, 23.25) * mm, "mid": v(38.94, 23.69) * mm, "end": v(38.5, 24.75) * mm});
            skArc(sketch, "E175.MirrorCS", {"start": v(46.14, 40.8) * mm, "mid": v(45.63, 42.48) * mm, "end": v(47.05, 43.5) * mm});
            skArc(sketch, "E176.MirrorCS", {"start": v(63.5, 43.5) * mm, "mid": v(64.56, 43.06) * mm, "end": v(65, 42) * mm});
            skLineSegment(sketch, "E177.MirrorCS", {"start": v(38.5, 43.5) * mm, "end": v(38.5, 40.35) * mm, "construction": true});
            skArc(sketch, "E178.MirrorCS", {"start": v(38.5, 37.32) * mm, "mid": v(39.34, 38.66) * mm, "end": v(40.91, 38.51) * mm});
            skArc(sketch, "E179.MirrorCS", {"start": v(65, 29.43) * mm, "mid": v(64.16, 28.09) * mm, "end": v(62.59, 28.24) * mm});
            skArc(sketch, "E180.MirrorCS", {"start": v(57.36, 25.94) * mm, "mid": v(57.87, 24.27) * mm, "end": v(56.45, 23.25) * mm});
            skPoint(sketch, "E181.MirrorP", {"position": v(51.75, 33.37) * mm});
            skPoint(sketch, "E182.MirrorP", {"position": v(38.5, 23.25) * mm});
            skLineSegment(sketch, "E183.MirrorCS", {"start": v(38.5, 43.5) * mm, "end": v(65, 23.25) * mm, "construction": true});
            skLineSegment(sketch, "E184.MirrorCS", {"start": v(65, 23.25) * mm, "end": v(60.88, 23.25) * mm, "construction": true});
            skLineSegment(sketch, "E185.MirrorCS", {"start": v(40.91, 38.51) * mm, "end": v(57.36, 25.94) * mm});
            skPoint(sketch, "E186.MirrorP", {"position": v(38.5, 40.35) * mm});
            skLineSegment(sketch, "E187.MirrorCS", {"start": v(62.59, 28.24) * mm, "end": v(46.14, 40.8) * mm});
            skPoint(sketch, "E188.MirrorP", {"position": v(60.88, 23.25) * mm});
            skLineSegment(sketch, "E189.MirrorCS", {"start": v(65, 29.43) * mm, "end": v(65, 42) * mm});
            skLineSegment(sketch, "E190.MirrorCS", {"start": v(38.5, 37.32) * mm, "end": v(38.5, 24.75) * mm});
            skLineSegment(sketch, "E191.MirrorCS", {"start": v(47.05, 43.5) * mm, "end": v(63.5, 43.5) * mm});
            skLineSegment(sketch, "E192.MirrorCS", {"start": v(56.45, 23.25) * mm, "end": v(40, 23.25) * mm});
            skSolve(sketch);
        }
        {
            var Q0;
            {var subQ1=sQuery(id+"F15.wireOp",EDGE,"E174.MirrorCS");var subQ5=makeQuery(id+"F15.imprint","IMPRINT",EDGE,{"derivedFrom":subQ1});var subQ8=sQuery(id+"F15.wireOp",EDGE,"E145.MirrorCS");var subQ14=makeQuery(id+"F15.imprint","IMPRINT",EDGE,{"derivedFrom":subQ8});var subQ17=sQuery(id+"F15.wireOp",EDGE,"E142.MirrorCS");Q0=qUnion([makeQuery(id+"F15.imprint","IMPRINT",FACE,{"disambiguationData":[TD([[makeQuery(id+"F15.imprint","IMPRINT",EDGE,{"derivedFrom":sQuery(id+"F15.wireOp",EDGE,"E117")}),-1.0]])]}),makeQuery(id+"F15.imprint","IMPRINT",FACE,{"disambiguationData":[TD([[makeQuery(id+"F15.imprint","IMPRINT",EDGE,{"derivedFrom":sQuery(id+"F15.wireOp",EDGE,"E172.1.0")}),1.0]])]}),makeQuery(id+"F15.imprint","IMPRINT",FACE,{"disambiguationData":[TD([[subQ14,-1.0]])]}),makeQuery(id+"F15.imprint","IMPRINT",FACE,{"disambiguationData":[TD([[makeQuery(id+"F15.imprint","IMPRINT",EDGE,{"derivedFrom":sQuery(id+"F15.wireOp",EDGE,"E164")}),1.0]])]}),makeQuery(id+"F15.imprint","IMPRINT",FACE,{"disambiguationData":[TD([[makeQuery(id+"F15.imprint","IMPRINT",EDGE,{"derivedFrom":subQ17}),-1.0]])]}),makeQuery(id+"F15.imprint","IMPRINT",FACE,{"disambiguationData":[TD([[subQ5,1.0]])]}),makeQuery(id+"F15.imprint","IMPRINT",FACE,{"disambiguationData":[TD([[makeQuery(id+"F15.imprint","IMPRINT",EDGE,{"derivedFrom":sQuery(id+"F15.wireOp",EDGE,"E175.MirrorCS")}),-1.0]])]}),makeQuery(id+"F15.imprint","IMPRINT",FACE,{"disambiguationData":[TD([[makeQuery(id+"F15.imprint","IMPRINT",EDGE,{"derivedFrom":sQuery(id+"F15.wireOp",EDGE,"E116")}),1.0]])]}),makeQuery(id+"F15.imprint","IMPRINT",FACE,{"disambiguationData":[TD([[subQ14,1.0]])]}),makeQuery(id+"F15.imprint","IMPRINT",FACE,{"disambiguationData":[TD([[subQ5,-1.0]])]})]);}
            extrude(context, id + "F16", {"entities" : qUnion([Q0]), "operationType" : NewBodyOperationType.REMOVE, "oppositeDirection" : true, "depth" : 25 * mm, "offsetDistance" : 25 * mm});
        }
        {
            var Q0;
            Q0=makeQuery(id+"F14.boolean.opBoolean","COPY",EDGE,{"derivedFrom":makeQuery(id+"F14.opExtrude","SWEPT_EDGE",EDGE,{"disambiguationData":[OSD([sQuery(id+"F13.wireOp",EDGE,"E68"),sQuery(id+"F13.wireOp",EDGE,"E69")])]})});
            fillet(context, id + "F17", {"entities" : qUnion([Q0]), "radius" : 1.5 * mm, "tangentPropagation" : true, "allowEdgeOverflow" : false});
        }
        {
            var Q0;
            Q0=makeQuery(id+"F14.boolean.opBoolean","COPY",EDGE,{"derivedFrom":makeQuery(id+"F14.opExtrude","SWEPT_EDGE",EDGE,{"disambiguationData":[OSD([sQuery(id+"F13.wireOp",EDGE,"E68"),sQuery(id+"F13.wireOp",EDGE,"E84")])]})});
            var Q1;
            Q1=makeQuery(id+"F14.boolean.opBoolean","COPY",EDGE,{"derivedFrom":makeQuery(id+"F14.opExtrude","SWEPT_EDGE",EDGE,{"disambiguationData":[OSD([sQuery(id+"F13.wireOp",EDGE,"E62"),sQuery(id+"F13.wireOp",EDGE,"E65")])]})});
            var Q2;
            Q2=makeQuery(id+"F14.boolean.opBoolean","COPY",EDGE,{"derivedFrom":makeQuery(id+"F14.opExtrude","SWEPT_EDGE",EDGE,{"disambiguationData":[OSD([sQuery(id+"F13.wireOp",EDGE,"E106"),sQuery(id+"F13.wireOp",EDGE,"E109")])]})});
            fillet(context, id + "F18", {"entities" : qUnion([Q0, Q1, Q2]), "radius" : 1.5 * mm, "tangentPropagation" : true, "allowEdgeOverflow" : false});
        }
        {
            var Q0;
            Q0=makeQuery(id+"F14.boolean.opBoolean","COPY",EDGE,{"derivedFrom":makeQuery(id+"F14.opExtrude","SWEPT_EDGE",EDGE,{"disambiguationData":[OSD([sQuery(id+"F13.wireOp",EDGE,"E78.MirrorCS"),sQuery(id+"F13.wireOp",EDGE,"E83.MirrorCS")])]})});
            var Q1;
            Q1=makeQuery(id+"F14.boolean.opBoolean","COPY",EDGE,{"derivedFrom":makeQuery(id+"F14.opExtrude","SWEPT_EDGE",EDGE,{"disambiguationData":[OSD([sQuery(id+"F13.wireOp",EDGE,"E63"),sQuery(id+"F13.wireOp",EDGE,"E83.MirrorCS"),sQuery(id+"F13.wireOp",EDGE,"E111")])]})});
            var Q2;
            {var subQ0=sQuery(id+"F13.wireOp",EDGE,"E58");Q2=qUnion([makeQuery(id+"F14.boolean.opBoolean","COPY",EDGE,{"derivedFrom":makeQuery(id+"F14.opExtrude","SWEPT_EDGE",EDGE,{"disambiguationData":[OSD([subQ0,sQuery(id+"F13.wireOp",EDGE,"E70")])]})}),makeQuery(id+"F14.boolean.opBoolean","COPY",EDGE,{"derivedFrom":makeQuery(id+"F14.opExtrude","SWEPT_EDGE",EDGE,{"disambiguationData":[OSD([subQ0,sQuery(id+"F13.wireOp",EDGE,"E74.MirrorCS")])]})})]);}
            var Q3;
            Q3=makeQuery(id+"F14.boolean.opBoolean","COPY",EDGE,{"derivedFrom":makeQuery(id+"F14.opExtrude","SWEPT_EDGE",EDGE,{"disambiguationData":[OSD([sQuery(id+"F13.wireOp",EDGE,"E58"),sQuery(id+"F13.wireOp",EDGE,"E74.MirrorCS")])]})});
            var Q4;
            Q4=makeQuery(id+"F14.boolean.opBoolean","COPY",EDGE,{"derivedFrom":makeQuery(id+"F14.opExtrude","SWEPT_EDGE",EDGE,{"disambiguationData":[OSD([sQuery(id+"F13.wireOp",EDGE,"E75.MirrorCS"),sQuery(id+"F13.wireOp",EDGE,"E78.MirrorCS")])]})});
            var Q5;
            Q5=makeQuery(id+"F14.boolean.opBoolean","COPY",EDGE,{"derivedFrom":makeQuery(id+"F14.opExtrude","SWEPT_EDGE",EDGE,{"disambiguationData":[OSD([sQuery(id+"F13.wireOp",EDGE,"E58"),sQuery(id+"F13.wireOp",EDGE,"E74.MirrorCS")])]})});
            var Q6;
            Q6=makeQuery(id+"F14.boolean.opBoolean","COPY",EDGE,{"derivedFrom":makeQuery(id+"F14.opExtrude","SWEPT_EDGE",EDGE,{"disambiguationData":[OSD([sQuery(id+"F13.wireOp",EDGE,"E75.MirrorCS"),sQuery(id+"F13.wireOp",EDGE,"E76.MirrorCS")])]})});
            var Q7;
            Q7=makeQuery(id+"F14.boolean.opBoolean","COPY",EDGE,{"derivedFrom":makeQuery(id+"F14.opExtrude","SWEPT_EDGE",EDGE,{"disambiguationData":[OSD([sQuery(id+"F13.wireOp",EDGE,"E76.MirrorCS"),sQuery(id+"F13.wireOp",EDGE,"E83.MirrorCS")])]})});
            var Q8;
            Q8=makeQuery(id+"F14.boolean.opBoolean","COPY",EDGE,{"derivedFrom":makeQuery(id+"F14.opExtrude","SWEPT_EDGE",EDGE,{"disambiguationData":[OSD([sQuery(id+"F13.wireOp",EDGE,"E61"),sQuery(id+"F13.wireOp",EDGE,"E87")])]})});
            var Q9;
            Q9=makeQuery(id+"F14.boolean.opBoolean","COPY",EDGE,{"derivedFrom":makeQuery(id+"F14.opExtrude","SWEPT_EDGE",EDGE,{"disambiguationData":[OSD([sQuery(id+"F2.wireOp",EDGE,"E5.1"),sQuery(id+"F13.wireOp",EDGE,"E61"),sQuery(id+"F13.wireOp",EDGE,"E92")])]})});
            var Q10;
            Q10=makeQuery(id+"F14.boolean.opBoolean","COPY",EDGE,{"derivedFrom":makeQuery(id+"F14.opExtrude","SWEPT_EDGE",EDGE,{"disambiguationData":[OSD([sQuery(id+"F2.wireOp",EDGE,"E5.2"),sQuery(id+"F13.wireOp",EDGE,"E99"),sQuery(id+"F13.wireOp",EDGE,"E101")])]})});
            var Q11;
            Q11=makeQuery(id+"F14.boolean.opBoolean","COPY",EDGE,{"derivedFrom":makeQuery(id+"F14.opExtrude","SWEPT_EDGE",EDGE,{"disambiguationData":[OSD([sQuery(id+"F2.wireOp",EDGE,"E5.2"),sQuery(id+"F13.wireOp",EDGE,"E92"),sQuery(id+"F13.wireOp",EDGE,"E93")])]})});
            var Q12;
            Q12=makeQuery(id+"F14.boolean.opBoolean","COPY",EDGE,{"derivedFrom":makeQuery(id+"F14.opExtrude","SWEPT_EDGE",EDGE,{"disambiguationData":[OSD([sQuery(id+"F13.wireOp",EDGE,"E101"),sQuery(id+"F13.wireOp",EDGE,"E102")])]})});
            var Q13;
            Q13=makeQuery(id+"F14.boolean.opBoolean","COPY",EDGE,{"derivedFrom":makeQuery(id+"F14.opExtrude","SWEPT_EDGE",EDGE,{"disambiguationData":[OSD([sQuery(id+"F13.wireOp",EDGE,"E100"),sQuery(id+"F13.wireOp",EDGE,"E102")])]})});
            var Q14;
            Q14=makeQuery(id+"F14.boolean.opBoolean","COPY",EDGE,{"derivedFrom":makeQuery(id+"F14.opExtrude","SWEPT_EDGE",EDGE,{"disambiguationData":[OSD([sQuery(id+"F13.wireOp",EDGE,"E99"),sQuery(id+"F13.wireOp",EDGE,"E100")])]})});
            var Q15;
            Q15=makeQuery(id+"F14.boolean.opBoolean","COPY",EDGE,{"derivedFrom":makeQuery(id+"F14.opExtrude","SWEPT_EDGE",EDGE,{"disambiguationData":[OSD([sQuery(id+"F13.wireOp",EDGE,"E95"),sQuery(id+"F13.wireOp",EDGE,"E98")])]})});
            var Q16;
            Q16=makeQuery(id+"F14.boolean.opBoolean","COPY",EDGE,{"derivedFrom":makeQuery(id+"F14.opExtrude","SWEPT_EDGE",EDGE,{"disambiguationData":[OSD([sQuery(id+"F13.wireOp",EDGE,"E88"),sQuery(id+"F13.wireOp",EDGE,"E89")])]})});
            var Q17;
            Q17=makeQuery(id+"F14.boolean.opBoolean","COPY",EDGE,{"derivedFrom":makeQuery(id+"F14.opExtrude","SWEPT_EDGE",EDGE,{"disambiguationData":[OSD([sQuery(id+"F13.wireOp",EDGE,"E89"),sQuery(id+"F13.wireOp",EDGE,"E90")])]})});
            var Q18;
            Q18=makeQuery(id+"F14.boolean.opBoolean","COPY",EDGE,{"derivedFrom":makeQuery(id+"F14.opExtrude","SWEPT_EDGE",EDGE,{"disambiguationData":[OSD([sQuery(id+"F13.wireOp",EDGE,"E97"),sQuery(id+"F13.wireOp",EDGE,"E98")])]})});
            var Q19;
            Q19=makeQuery(id+"F14.boolean.opBoolean","COPY",EDGE,{"derivedFrom":makeQuery(id+"F14.opExtrude","SWEPT_EDGE",EDGE,{"disambiguationData":[OSD([sQuery(id+"F13.wireOp",EDGE,"E96"),sQuery(id+"F13.wireOp",EDGE,"E97")])]})});
            var Q20;
            Q20=makeQuery(id+"F14.boolean.opBoolean","COPY",EDGE,{"derivedFrom":makeQuery(id+"F14.opExtrude","SWEPT_EDGE",EDGE,{"disambiguationData":[OSD([sQuery(id+"F2.wireOp",EDGE,"E5.0"),sQuery(id+"F13.wireOp",EDGE,"E95"),sQuery(id+"F13.wireOp",EDGE,"E96")])]})});
            var Q21;
            Q21=makeQuery(id+"F14.boolean.opBoolean","COPY",EDGE,{"derivedFrom":makeQuery(id+"F14.opExtrude","SWEPT_EDGE",EDGE,{"disambiguationData":[OSD([sQuery(id+"F2.wireOp",EDGE,"E5.0"),sQuery(id+"F13.wireOp",EDGE,"E90"),sQuery(id+"F13.wireOp",EDGE,"E91")])]})});
            var Q22;
            Q22=makeQuery(id+"F14.boolean.opBoolean","COPY",EDGE,{"derivedFrom":makeQuery(id+"F14.opExtrude","SWEPT_EDGE",EDGE,{"disambiguationData":[OSD([sQuery(id+"F2.wireOp",EDGE,"E5.1"),sQuery(id+"F13.wireOp",EDGE,"E60"),sQuery(id+"F13.wireOp",EDGE,"E91")])]})});
            var Q23;
            Q23=makeQuery(id+"F14.boolean.opBoolean","COPY",EDGE,{"derivedFrom":makeQuery(id+"F14.opExtrude","SWEPT_EDGE",EDGE,{"disambiguationData":[OSD([sQuery(id+"F13.wireOp",EDGE,"E60"),sQuery(id+"F13.wireOp",EDGE,"E88")])]})});
            fillet(context, id + "F19", {"entities" : qUnion([Q0, Q1, Q2, Q3, Q4, Q5, Q6, Q7, Q8, Q9, Q10, Q11, Q12, Q13, Q14, Q15, Q16, Q17, Q18, Q19, Q20, Q21, Q22, Q23]), "radius" : 1.5 * mm, "tangentPropagation" : true, "allowEdgeOverflow" : false});
        }
        {
            var Q0;
            Q0=makeQuery(id+"F14.boolean.opBoolean","COPY",EDGE,{"derivedFrom":makeQuery(id+"F14.opExtrude","SWEPT_EDGE",EDGE,{"disambiguationData":[OSD([sQuery(id+"F13.wireOp",EDGE,"E87"),sQuery(id+"F13.wireOp",EDGE,"E94")])]})});
            var Q1;
            Q1=makeQuery(id+"F14.boolean.opBoolean","COPY",EDGE,{"derivedFrom":makeQuery(id+"F14.opExtrude","SWEPT_EDGE",EDGE,{"disambiguationData":[OSD([sQuery(id+"F13.wireOp",EDGE,"E93"),sQuery(id+"F13.wireOp",EDGE,"E94")])]})});
            fillet(context, id + "F20", {"entities" : qUnion([Q0, Q1]), "radius" : 1.5 * mm, "tangentPropagation" : true, "allowEdgeOverflow" : false});
        }
        {
            var Q0;
            Q0=makeQuery(id+"F14.boolean.opBoolean","COPY",EDGE,{"derivedFrom":makeQuery(id+"F14.opExtrude","SWEPT_EDGE",EDGE,{"disambiguationData":[OSD([sQuery(id+"F13.wireOp",EDGE,"E106"),sQuery(id+"F13.wireOp",EDGE,"E109")])]})});
            var Q1;
            Q1=makeQuery(id+"F14.boolean.opBoolean","COPY",EDGE,{"derivedFrom":makeQuery(id+"F14.opExtrude","SWEPT_EDGE",EDGE,{"disambiguationData":[OSD([sQuery(id+"F13.wireOp",EDGE,"E83.MirrorCS"),sQuery(id+"F13.wireOp",EDGE,"E109")])]})});
            var Q2;
            Q2=makeQuery(id+"F14.boolean.opBoolean","COPY",EDGE,{"derivedFrom":makeQuery(id+"F14.opExtrude","SWEPT_EDGE",EDGE,{"disambiguationData":[OSD([sQuery(id+"F13.wireOp",EDGE,"E110"),sQuery(id+"F13.wireOp",EDGE,"E111")])]})});
            fillet(context, id + "F21", {"entities" : qUnion([Q0, Q1, Q2]), "radius" : 1 * mm, "tangentPropagation" : true, "allowEdgeOverflow" : false});
        }
        {
            var Q0;
            Q0=makeQuery(id+"F13.imprint","IMPRINT",FACE,{"disambiguationData":[TD([[makeQuery(id+"F13.imprint","IMPRINT",EDGE,{"derivedFrom":sQuery(id+"F13.wireOp",EDGE,"E60")}),-1.0]])]});
            var sketch = newSketch(context, id + "F22", { "sketchPlane" : qUnion([Q0])});
            skLineSegment(sketch, "E193", {"start": v(-75, 60) * mm, "end": v(-71, 56) * mm});
            skLineSegment(sketch, "E194", {"start": v(-71, 56) * mm, "end": v(-71, -56) * mm});
            skLineSegment(sketch, "E195", {"start": v(-71, -56) * mm, "end": v(-75, -60) * mm});
            skLineSegment(sketch, "E196", {"start": v(-75, -60) * mm, "end": v(-75, 60) * mm});
            skSolve(sketch);
        }
        {
            var Q0;
            Q0 = qSketchRegion(id + "F22", true);
            extrude(context, id + "F23", {"entities" : qUnion([Q0]), "operationType" : NewBodyOperationType.REMOVE, "oppositeDirection" : true, "depth" : 25 * mm, "offsetDistance" : 25 * mm});
        }
        {
            var Q0;
            Q0=makeQuery(id+"F13.imprint","IMPRINT",FACE,{"disambiguationData":[TD([[makeQuery(id+"F13.imprint","IMPRINT",EDGE,{"derivedFrom":sQuery(id+"F13.wireOp",EDGE,"E60")}),-1.0]])]});
            var sketch = newSketch(context, id + "F24", { "sketchPlane" : qUnion([Q0])});
            skLineSegment(sketch, "E197", {"start": v(-65.27, -61.73) * mm, "end": v(-75, -60) * mm});
            skLineSegment(sketch, "E198", {"start": v(-75, -60) * mm, "end": v(-72.29, -52.52) * mm});
            skLineSegment(sketch, "E199", {"start": v(-72.29, -52.52) * mm, "end": v(-65.27, -61.73) * mm});
            skLineSegment(sketch, "E200.MirrorCS", {"start": v(-72.29, 52.52) * mm, "end": v(-65.27, 61.73) * mm});
            skLineSegment(sketch, "E201.MirrorCS", {"start": v(-65.27, 61.73) * mm, "end": v(-75, 60) * mm});
            skLineSegment(sketch, "E202.MirrorCS", {"start": v(-75, 60) * mm, "end": v(-72.29, 52.52) * mm});
            skSolve(sketch);
        }
        {
            var Q0;
            Q0 = qSketchRegion(id + "F24", true);
            extrude(context, id + "F25", {"entities" : qUnion([Q0]), "operationType" : NewBodyOperationType.REMOVE, "oppositeDirection" : true, "depth" : 25 * mm, "offsetDistance" : 25 * mm});
        }
    });
